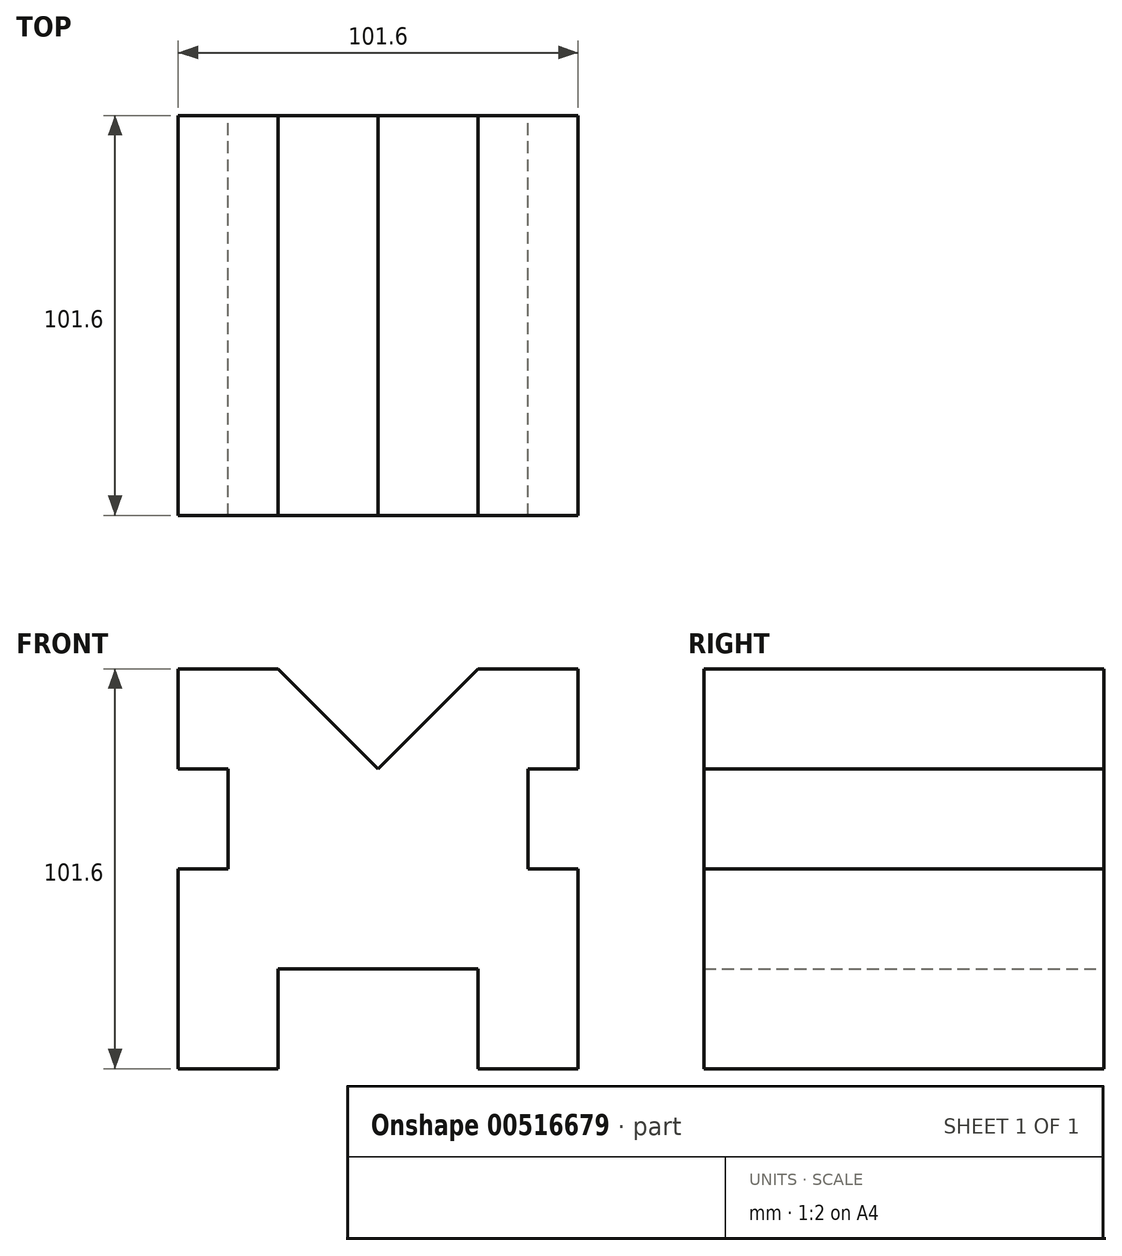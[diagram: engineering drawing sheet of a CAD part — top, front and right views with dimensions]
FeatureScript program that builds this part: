
annotation { "Feature Type Name" : "Feature", "Feature Type Description" : "" }
export const myFeature = defineFeature(function(context is Context, id is Id, definition is map)
    precondition{}
    {
        {
            var Q0;
            Q0=qCreatedBy(makeId("Front.planeOp"),FACE);
            var sketch = newSketch(context, id + "F0", { "sketchPlane" : qUnion([Q0])});
            skLineSegment(sketch, "E0", {"start": v(-50.8, 0) * mm, "end": v(-50.8, -50.8) * mm});
            skLineSegment(sketch, "E1", {"start": v(-50.8, -50.8) * mm, "end": v(-25.4, -50.8) * mm});
            skLineSegment(sketch, "E2", {"start": v(-25.4, -25.4) * mm, "end": v(-25.4, -50.8) * mm});
            skLineSegment(sketch, "E3", {"start": v(-25.4, -25.4) * mm, "end": v(25.4, -25.4) * mm});
            skLineSegment(sketch, "E4", {"start": v(25.4, -50.8) * mm, "end": v(25.4, -25.4) * mm});
            skLineSegment(sketch, "E5", {"start": v(25.4, -50.8) * mm, "end": v(50.8, -50.8) * mm});
            skLineSegment(sketch, "E6", {"start": v(50.8, -50.8) * mm, "end": v(50.8, 0) * mm});
            skLineSegment(sketch, "E7", {"start": v(50.8, 0) * mm, "end": v(38.1, 0) * mm});
            skLineSegment(sketch, "E8", {"start": v(38.1, 25.4) * mm, "end": v(38.1, 0) * mm});
            skLineSegment(sketch, "E9", {"start": v(38.1, 25.4) * mm, "end": v(50.8, 25.4) * mm});
            skLineSegment(sketch, "E10", {"start": v(50.8, 50.8) * mm, "end": v(50.8, 25.4) * mm});
            skLineSegment(sketch, "E11", {"start": v(50.8, 50.8) * mm, "end": v(25.4, 50.8) * mm});
            skLineSegment(sketch, "E12", {"start": v(25.4, 50.8) * mm, "end": v(0, 25.4) * mm});
            skLineSegment(sketch, "E13", {"start": v(0, 25.4) * mm, "end": v(-25.4, 50.8) * mm});
            skLineSegment(sketch, "E14", {"start": v(-25.4, 50.8) * mm, "end": v(-50.8, 50.8) * mm});
            skLineSegment(sketch, "E15", {"start": v(-50.8, 50.8) * mm, "end": v(-50.8, 25.4) * mm});
            skLineSegment(sketch, "E16", {"start": v(-50.8, 25.4) * mm, "end": v(-38.1, 25.4) * mm});
            skLineSegment(sketch, "E17", {"start": v(-38.1, 25.4) * mm, "end": v(-38.1, 0) * mm});
            skLineSegment(sketch, "E18", {"start": v(-38.1, 0) * mm, "end": v(-50.8, 0) * mm});
            skSolve(sketch);
        }
        {
            var Q0;
            Q0=makeQuery(id+"F0.imprint","IMPRINT",FACE,{"disambiguationData":[TD([[makeQuery(id+"F0.imprint","IMPRINT",EDGE,{"derivedFrom":sQuery(id+"F0.wireOp",EDGE,"E0")}),1.0]])]});
            extrude(context, id + "F1", {"entities" : qUnion([Q0]), "depth" : 101.6 * mm, "offsetDistance" : 25.4 * mm});
        }
    });
